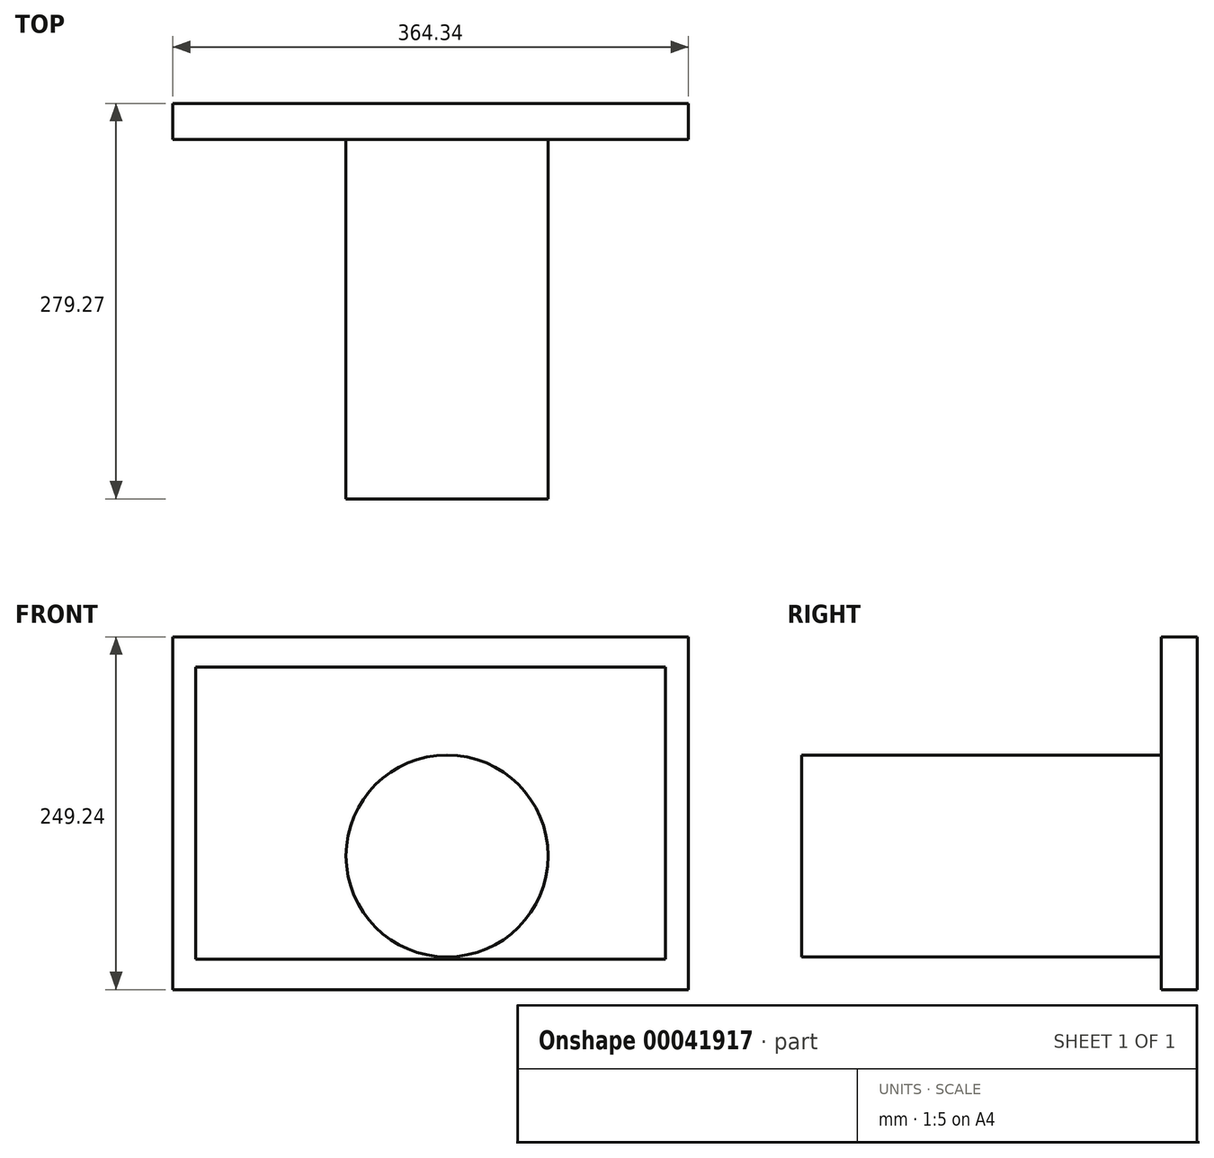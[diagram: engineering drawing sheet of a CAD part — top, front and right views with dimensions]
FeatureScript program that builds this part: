
annotation { "Feature Type Name" : "Feature", "Feature Type Description" : "" }
export const myFeature = defineFeature(function(context is Context, id is Id, definition is map)
    precondition{}
    {
        {
            var Q0;
            Q0=qCreatedBy(makeId("Front.planeOp"),FACE);
            var sketch = newSketch(context, id + "F0", { "sketchPlane" : qUnion([Q0])});
            skLineSegment(sketch, "E0.rect.bottom", {"start": v(182.17, 124.62) * mm, "end": v(-182.17, 124.62) * mm});
            skLineSegment(sketch, "E0.rect.top", {"start": v(182.17, -124.62) * mm, "end": v(-182.17, -124.62) * mm});
            skLineSegment(sketch, "E0.rect.left", {"start": v(182.17, 124.62) * mm, "end": v(182.17, -124.62) * mm});
            skLineSegment(sketch, "E0.rect.right", {"start": v(-182.17, 124.62) * mm, "end": v(-182.17, -124.62) * mm});
            skPoint(sketch, "E0.rect.middle", {"position": v(0, 0) * mm});
            skLineSegment(sketch, "E1.rect.bottom", {"start": v(165.9, 103.19) * mm, "end": v(-165.9, 103.19) * mm, "construction": true});
            skLineSegment(sketch, "E1.rect.top", {"start": v(165.9, -103.19) * mm, "end": v(-165.9, -103.19) * mm, "construction": true});
            skLineSegment(sketch, "E1.rect.left", {"start": v(165.9, 103.19) * mm, "end": v(165.9, -103.19) * mm, "construction": true});
            skLineSegment(sketch, "E1.rect.right", {"start": v(-165.9, 103.19) * mm, "end": v(-165.9, -103.19) * mm, "construction": true});
            skSolve(sketch);
        }
        {
            var Q0;
            Q0=makeQuery(id+"F0.imprint","IMPRINT",FACE,{"disambiguationData":[TD([[makeQuery(id+"F0.imprint","IMPRINT",EDGE,{"derivedFrom":sQuery(id+"F0.wireOp",EDGE,"E0.rect.bottom")}),1.0]])]});
            extrude(context, id + "F1", {"entities" : qUnion([Q0]), "depth" : 25.4 * mm});
        }
        {
            var Q0;
            Q0=makeQuery(id+"F1.opExtrude","CAP_FACE",FACE,{"disambiguationData":[OSD([sQuery(id+"F0.wireOp",EDGE,"E0.rect.bottom"),sQuery(id+"F0.wireOp",EDGE,"E0.rect.top"),sQuery(id+"F0.wireOp",EDGE,"E0.rect.left"),sQuery(id+"F0.wireOp",EDGE,"E0.rect.right")])],"isStart":false});
            var sketch = newSketch(context, id + "F2", { "sketchPlane" : qUnion([Q0])});
            skLineSegment(sketch, "E2.0", {"start": v(-165.9, 103.19) * mm, "end": v(-165.9, -103.19) * mm});
            skLineSegment(sketch, "E2.1", {"start": v(165.9, 103.19) * mm, "end": v(-165.9, 103.19) * mm});
            skLineSegment(sketch, "E2.2", {"start": v(165.9, 103.19) * mm, "end": v(165.9, -103.19) * mm});
            skLineSegment(sketch, "E2.3", {"start": v(165.9, -103.19) * mm, "end": v(-165.9, -103.19) * mm});
            skSolve(sketch);
        }
        {
            var Q0;
            Q0 = qSketchRegion(id + "F2", true);
            extrude(context, id + "F3", {"entities" : qUnion([Q0]), "operationType" : NewBodyOperationType.REMOVE, "oppositeDirection" : true, "depth" : 0.13 * mm});
        }
        {
            var Q0;
            Q0=makeQuery(id+"F3.boolean.opBoolean","COPY",FACE,{"derivedFrom":makeQuery(id+"F3.opExtrude","CAP_FACE",FACE,{"disambiguationData":[OSD([sQuery(id+"F2.wireOp",EDGE,"E2.0"),sQuery(id+"F2.wireOp",EDGE,"E2.1"),sQuery(id+"F2.wireOp",EDGE,"E2.2"),sQuery(id+"F2.wireOp",EDGE,"E2.3")])],"isStart":false})});
            var sketch = newSketch(context, id + "F4", { "sketchPlane" : qUnion([Q0])});
            skCircle(sketch, "E3", {"center": v(11.56, -30.23) * mm, "radius": 71.32 * mm});
            skSolve(sketch);
        }
        {
            var Q0;
            Q0 = qSketchRegion(id + "F4", true);
            extrude(context, id + "F5", {"entities" : qUnion([Q0]), "operationType" : NewBodyOperationType.ADD, "depth" : 254 * mm});
        }
    });
